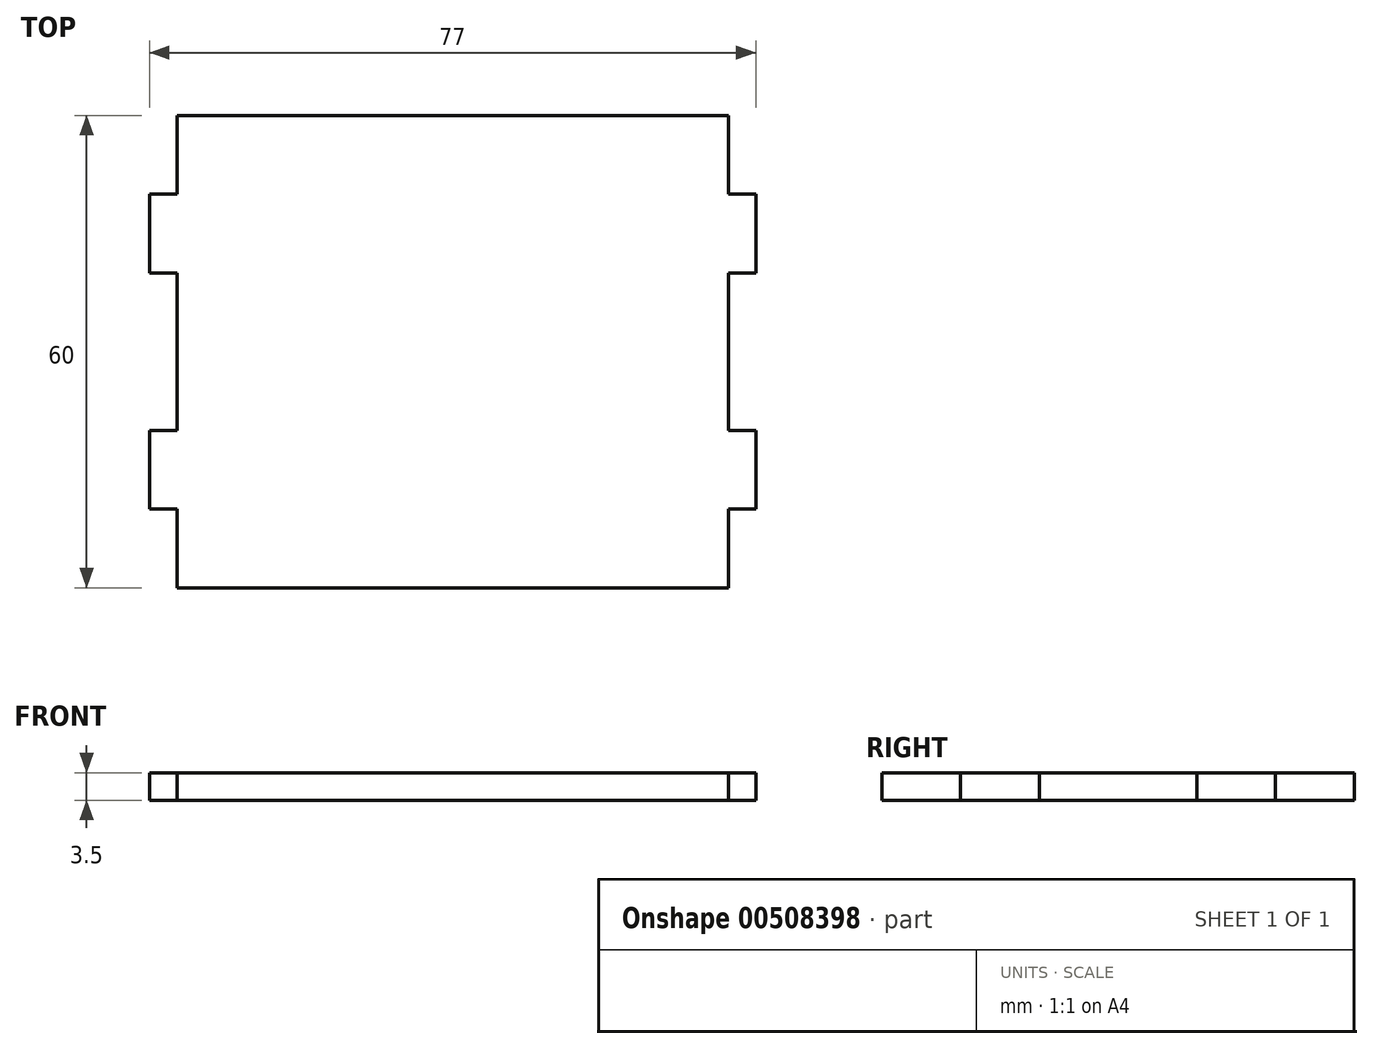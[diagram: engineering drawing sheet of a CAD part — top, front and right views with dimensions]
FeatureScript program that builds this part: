
annotation { "Feature Type Name" : "Feature", "Feature Type Description" : "" }
export const myFeature = defineFeature(function(context is Context, id is Id, definition is map)
    precondition{}
    {
        {
            var Q0;
            Q0=qCreatedBy(makeId("Top.planeOp"),FACE);
            var sketch = newSketch(context, id + "F0", { "sketchPlane" : qUnion([Q0])});
            skLineSegment(sketch, "E0.bottom", {"start": v(-35, 30) * mm, "end": v(35, 30) * mm});
            skLineSegment(sketch, "E0.top", {"start": v(-35, -30) * mm, "end": v(35, -30) * mm});
            skLineSegment(sketch, "E0.left", {"start": v(-35, 30) * mm, "end": v(-35, -30) * mm});
            skLineSegment(sketch, "E0.right", {"start": v(35, 30) * mm, "end": v(35, -30) * mm});
            skSolve(sketch);
        }
        {
            var Q0;
            Q0=makeQuery(id+"F0.imprint","IMPRINT",FACE,{"disambiguationData":[TD([[makeQuery(id+"F0.imprint","IMPRINT",EDGE,{"derivedFrom":sQuery(id+"F0.wireOp",EDGE,"E0.bottom")}),-1.0]])]});
            var Q1;
            Q1 = qSketchRegion(id + "F0", true);
            extrude(context, id + "F1", {"entities" : qUnion([Q0, Q1]), "depth" : 3.5 * mm, "offsetDistance" : 25 * mm});
        }
        {
            var Q0;
            Q0=makeQuery(id+"F1.opExtrude","SWEPT_FACE",FACE,{"disambiguationData":[OSD([sQuery(id+"F0.wireOp",EDGE,"E0.right")])]});
            var sketch = newSketch(context, id + "F2", { "sketchPlane" : qUnion([Q0])});
            skLineSegment(sketch, "E1", {"start": v(30, 0) * mm, "end": v(20, 0) * mm});
            skLineSegment(sketch, "E2", {"start": v(20, 0) * mm, "end": v(20, 3.5) * mm});
            skLineSegment(sketch, "E3", {"start": v(20, 3.5) * mm, "end": v(10, 3.5) * mm});
            skLineSegment(sketch, "E4", {"start": v(10, 3.5) * mm, "end": v(10, 0) * mm});
            skLineSegment(sketch, "E5", {"start": v(10, 0) * mm, "end": v(-10, 0) * mm});
            skLineSegment(sketch, "E6", {"start": v(-10, 0) * mm, "end": v(-10, 3.5) * mm});
            skLineSegment(sketch, "E7", {"start": v(-10, 3.5) * mm, "end": v(-20, 3.5) * mm});
            skLineSegment(sketch, "E8", {"start": v(-20, 3.5) * mm, "end": v(-20, 0) * mm});
            skSolve(sketch);
        }
        {
            var Q0;
            {var subQ0=sQuery(id+"F2.wireOp",EDGE,"E6");Q0=makeQuery(id+"F2.imprint","IMPRINT",FACE,{"disambiguationData":[TD([[makeQuery(id+"F2.imprint","IMPRINT",EDGE,{"derivedFrom":subQ0}),1.0]])]});}
            var Q1;
            {var subQ0=sQuery(id+"F2.wireOp",EDGE,"E2");Q1=makeQuery(id+"F2.imprint","IMPRINT",FACE,{"disambiguationData":[TD([[makeQuery(id+"F2.imprint","IMPRINT",EDGE,{"derivedFrom":subQ0}),1.0]])]});}
            extrude(context, id + "F3", {"entities" : qUnion([Q0, Q1]), "operationType" : NewBodyOperationType.ADD, "depth" : 3.5 * mm, "offsetDistance" : 25 * mm});
        }
        {
            var Q0;
            Q0=makeQuery(id+"F1.opExtrude","SWEPT_FACE",FACE,{"disambiguationData":[OSD([sQuery(id+"F0.wireOp",EDGE,"E0.left")])]});
            var sketch = newSketch(context, id + "F4", { "sketchPlane" : qUnion([Q0])});
            skLineSegment(sketch, "E9", {"start": v(-30, 3.5) * mm, "end": v(-20, 3.5) * mm});
            skLineSegment(sketch, "E10", {"start": v(-20, 3.5) * mm, "end": v(-20, 0) * mm});
            skLineSegment(sketch, "E11", {"start": v(-20, 0) * mm, "end": v(-10, 0) * mm});
            skLineSegment(sketch, "E12", {"start": v(-10, 0) * mm, "end": v(-10, 3.5) * mm});
            skLineSegment(sketch, "E13", {"start": v(-10, 3.5) * mm, "end": v(10, 3.5) * mm});
            skLineSegment(sketch, "E14", {"start": v(10, 3.5) * mm, "end": v(10, 0) * mm});
            skLineSegment(sketch, "E15", {"start": v(10, 0) * mm, "end": v(20, 0) * mm});
            skLineSegment(sketch, "E16", {"start": v(20, 0) * mm, "end": v(20, 3.5) * mm});
            skSolve(sketch);
        }
        {
            var Q0;
            {var subQ0=sQuery(id+"F4.wireOp",EDGE,"E10");Q0=makeQuery(id+"F4.imprint","IMPRINT",FACE,{"disambiguationData":[TD([[makeQuery(id+"F4.imprint","IMPRINT",EDGE,{"derivedFrom":subQ0}),1.0]])]});}
            var Q1;
            {var subQ0=sQuery(id+"F4.wireOp",EDGE,"E14");Q1=makeQuery(id+"F4.imprint","IMPRINT",FACE,{"disambiguationData":[TD([[makeQuery(id+"F4.imprint","IMPRINT",EDGE,{"derivedFrom":subQ0}),1.0]])]});}
            extrude(context, id + "F5", {"entities" : qUnion([Q0, Q1]), "operationType" : NewBodyOperationType.ADD, "depth" : 3.5 * mm, "offsetDistance" : 25 * mm});
        }
    });
